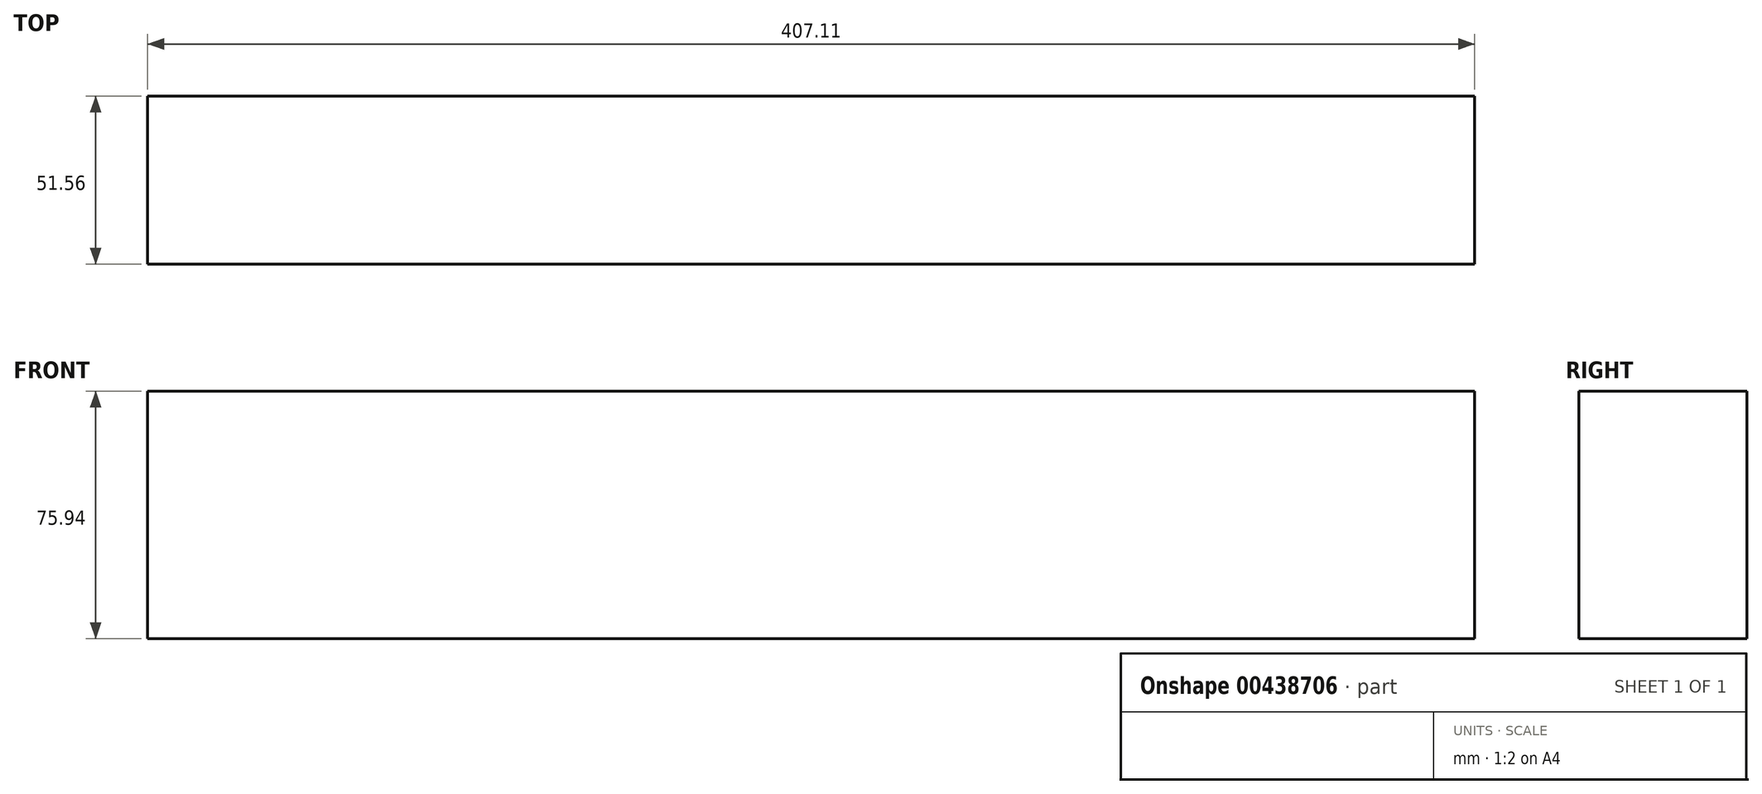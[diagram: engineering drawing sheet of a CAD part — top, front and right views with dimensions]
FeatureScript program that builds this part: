
annotation { "Feature Type Name" : "Feature", "Feature Type Description" : "" }
export const myFeature = defineFeature(function(context is Context, id is Id, definition is map)
    precondition{}
    {
        {
            var Q0;
            Q0=qCreatedBy(makeId("Front.planeOp"),FACE);
            var sketch = newSketch(context, id + "F0", { "sketchPlane" : qUnion([Q0])});
            skLineSegment(sketch, "E0", {"start": v(-189.63, -66.73) * mm, "end": v(217.48, -66.73) * mm});
            skLineSegment(sketch, "E1", {"start": v(-189.63, -66.73) * mm, "end": v(-189.63, 9.21) * mm});
            skLineSegment(sketch, "E2.bottom", {"start": v(217.48, -66.73) * mm, "end": v(-189.63, -66.73) * mm});
            skLineSegment(sketch, "E2.top", {"start": v(217.48, 9.21) * mm, "end": v(-189.63, 9.21) * mm});
            skLineSegment(sketch, "E2.left", {"start": v(217.48, -66.73) * mm, "end": v(217.48, 9.21) * mm});
            skSolve(sketch);
        }
        {
            var Q0;
            Q0 = qSketchRegion(id + "F0", true);
            extrude(context, id + "F1", {"entities" : qUnion([Q0]), "depth" : 51.56 * mm});
        }
    });
